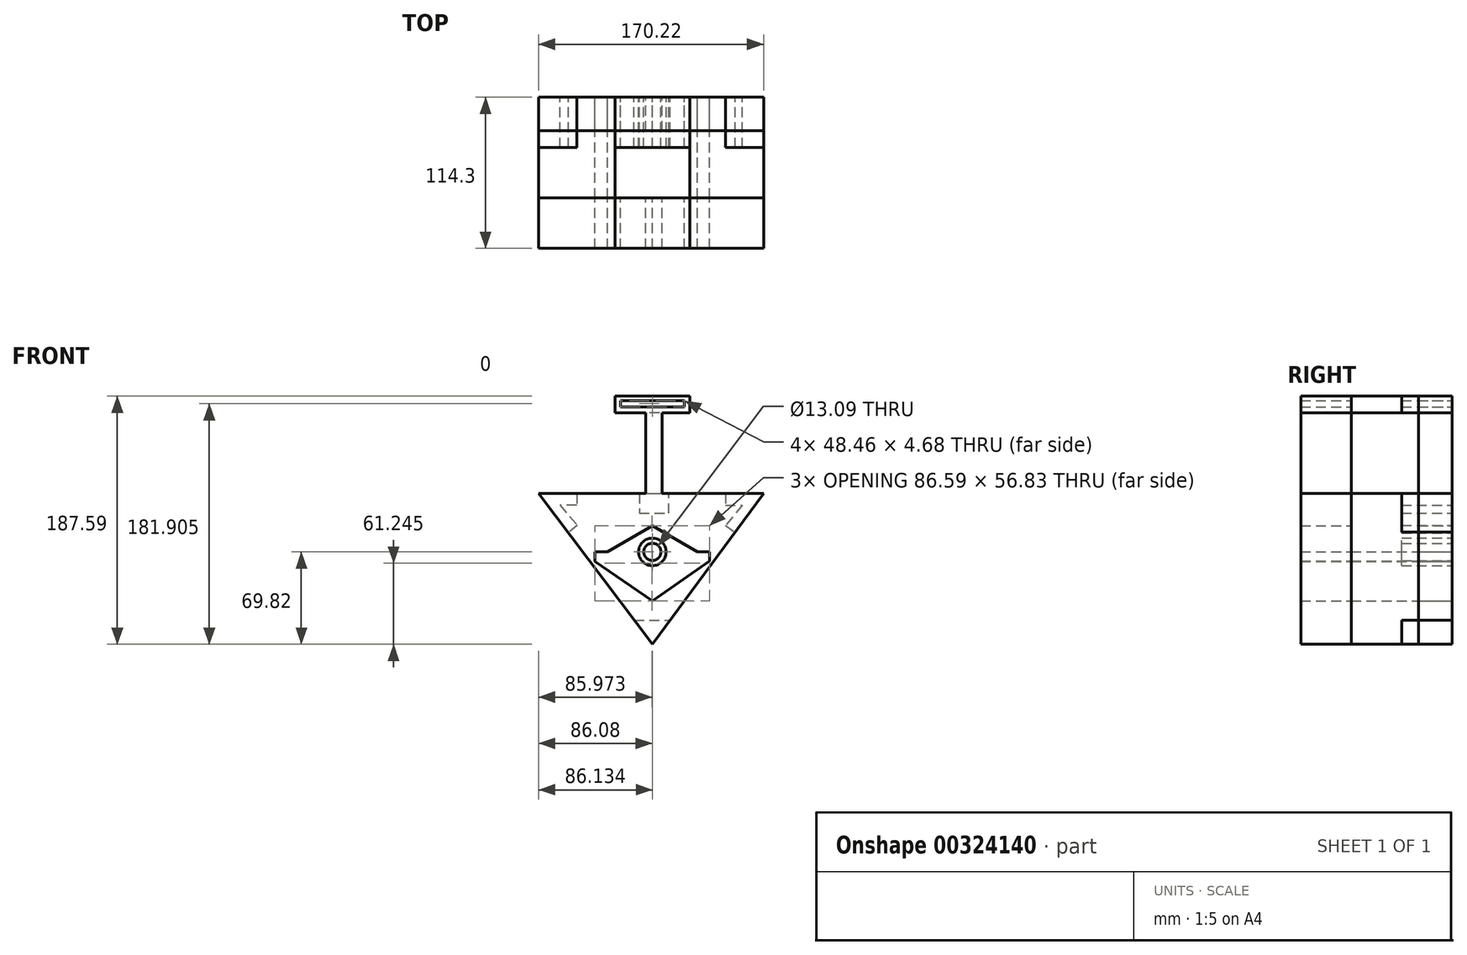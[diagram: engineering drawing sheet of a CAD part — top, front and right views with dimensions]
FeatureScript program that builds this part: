
annotation { "Feature Type Name" : "Feature", "Feature Type Description" : "" }
export const myFeature = defineFeature(function(context is Context, id is Id, definition is map)
    precondition{}
    {
        {
            var Q0;
            Q0=qCreatedBy(makeId("Front.planeOp"),FACE);
            var sketch = newSketch(context, id + "F0", { "sketchPlane" : qUnion([Q0])});
            skLineSegment(sketch, "E0", {"start": v(84.14, 44.25) * mm, "end": v(0, -69.82) * mm});
            skLineSegment(sketch, "E1", {"start": v(0, -69.82) * mm, "end": v(-86.08, 44.25) * mm});
            skLineSegment(sketch, "E2", {"start": v(-86.08, 44.25) * mm, "end": v(84.14, 44.25) * mm});
            skLineSegment(sketch, "E3", {"start": v(-13.76, -51.58) * mm, "end": v(13.45, -51.58) * mm});
            skLineSegment(sketch, "E4", {"start": v(55.26, 44.25) * mm, "end": v(55.26, 35.37) * mm});
            skLineSegment(sketch, "E5", {"start": v(55.26, 35.37) * mm, "end": v(67.96, 35.37) * mm});
            skLineSegment(sketch, "E6", {"start": v(67.96, 35.37) * mm, "end": v(55.3, 20.13) * mm});
            skLineSegment(sketch, "E7", {"start": v(55.3, 20.13) * mm, "end": v(62.45, 14.85) * mm});
            skLineSegment(sketch, "E8", {"start": v(-57.2, 44.25) * mm, "end": v(-57.2, 35.37) * mm});
            skLineSegment(sketch, "E9", {"start": v(-57.2, 35.37) * mm, "end": v(-69.9, 35.37) * mm});
            skLineSegment(sketch, "E10", {"start": v(-69.9, 35.37) * mm, "end": v(-56.76, 20.13) * mm});
            skLineSegment(sketch, "E11", {"start": v(-56.76, 20.13) * mm, "end": v(-63.5, 14.32) * mm});
            skCircle(sketch, "E12", {"center": v(0, 0) * mm, "radius": 10.43 * mm});
            skCircle(sketch, "E13", {"center": v(0, 0) * mm, "radius": 6.55 * mm});
            skLineSegment(sketch, "E14", {"start": v(-126.97, 0) * mm, "end": v(136.35, 0) * mm, "construction": true});
            skLineSegment(sketch, "E15", {"start": v(0, 91.75) * mm, "end": v(0, -85.84) * mm, "construction": true});
            skLineSegment(sketch, "E16", {"start": v(-9.84, 44.25) * mm, "end": v(-9.84, 29.26) * mm});
            skLineSegment(sketch, "E17", {"start": v(-9.84, 29.26) * mm, "end": v(12.4, 29.26) * mm});
            skLineSegment(sketch, "E18", {"start": v(12.4, 29.26) * mm, "end": v(12.4, 44.25) * mm});
            skPoint(sketch, "E19", {"position": v(0, 44.25) * mm});
            skLineSegment(sketch, "E20", {"start": v(-5.08, 44.25) * mm, "end": v(-5.08, 105.28) * mm});
            skLineSegment(sketch, "E21", {"start": v(-5.08, 105.28) * mm, "end": v(7.33, 105.28) * mm});
            skLineSegment(sketch, "E22", {"start": v(7.33, 105.28) * mm, "end": v(7.33, 44.25) * mm});
            skLineSegment(sketch, "E23", {"start": v(-5.08, 105.28) * mm, "end": v(-28.17, 105.28) * mm});
            skLineSegment(sketch, "E24", {"start": v(-28.17, 105.28) * mm, "end": v(-28.17, 117.77) * mm});
            skLineSegment(sketch, "E25", {"start": v(-28.17, 117.77) * mm, "end": v(28.31, 117.77) * mm});
            skLineSegment(sketch, "E26", {"start": v(28.31, 117.77) * mm, "end": v(28.31, 105.28) * mm});
            skLineSegment(sketch, "E27", {"start": v(28.31, 105.28) * mm, "end": v(7.33, 105.28) * mm});
            skLineSegment(sketch, "E28", {"start": v(-33.85, 0) * mm, "end": v(0, 19.84) * mm});
            skLineSegment(sketch, "E29", {"start": v(0, 19.84) * mm, "end": v(34, 0) * mm});
            skLineSegment(sketch, "E30", {"start": v(34, 0) * mm, "end": v(0, -20.6) * mm});
            skLineSegment(sketch, "E31", {"start": v(0, -20.6) * mm, "end": v(-33.85, 0) * mm});
            skLineSegment(sketch, "E32", {"start": v(-24.18, 114.42) * mm, "end": v(24.28, 114.42) * mm});
            skLineSegment(sketch, "E33", {"start": v(24.28, 114.42) * mm, "end": v(24.28, 109.75) * mm});
            skLineSegment(sketch, "E34", {"start": v(-24.18, 114.42) * mm, "end": v(-24.18, 109.75) * mm});
            skLineSegment(sketch, "E35", {"start": v(-24.18, 109.75) * mm, "end": v(24.28, 109.75) * mm});
            skLineSegment(sketch, "E36", {"start": v(-24.18, 44.25) * mm, "end": v(-24.18, 29.26) * mm});
            skLineSegment(sketch, "E37", {"start": v(-24.18, 29.26) * mm, "end": v(-45.5, 29.26) * mm});
            skLineSegment(sketch, "E38", {"start": v(-45.5, 29.26) * mm, "end": v(-33.83, 17.6) * mm});
            skLineSegment(sketch, "E39", {"start": v(-33.83, 17.6) * mm, "end": v(-48.6, 8.97) * mm});
            skLineSegment(sketch, "E40", {"start": v(-48.6, 8.97) * mm, "end": v(-33.85, 0) * mm});
            skLineSegment(sketch, "E41", {"start": v(-43.4, -7.1) * mm, "end": v(0, -36.99) * mm});
            skLineSegment(sketch, "E42", {"start": v(26.75, 44.25) * mm, "end": v(26.75, 29.26) * mm});
            skLineSegment(sketch, "E43", {"start": v(26.75, 29.26) * mm, "end": v(48.08, 29.26) * mm});
            skLineSegment(sketch, "E44", {"start": v(48.08, 29.26) * mm, "end": v(31.15, 15.8) * mm});
            skLineSegment(sketch, "E45", {"start": v(31.15, 15.8) * mm, "end": v(47.03, 11.32) * mm});
            skLineSegment(sketch, "E46", {"start": v(47.03, 11.32) * mm, "end": v(34, 0) * mm});
            skLineSegment(sketch, "E47", {"start": v(43.2, -6.78) * mm, "end": v(0, -36.99) * mm});
            skLineSegment(sketch, "E48", {"start": v(-43.4, -7.1) * mm, "end": v(-43.4, 0) * mm});
            skLineSegment(sketch, "E49", {"start": v(-43.4, 0) * mm, "end": v(-33.85, 0) * mm});
            skLineSegment(sketch, "E50", {"start": v(-41.23, 0) * mm, "end": v(-33.85, 0) * mm});
            skPoint(sketch, "E50.startSnap0", {"position": v(-41.23, 4.49) * mm});
            skLineSegment(sketch, "E51", {"start": v(43.2, -6.78) * mm, "end": v(43.2, 0) * mm});
            skLineSegment(sketch, "E52", {"start": v(43.2, 0) * mm, "end": v(34, 0) * mm});
            skLineSegment(sketch, "E53", {"start": v(-41.23, 0) * mm, "end": v(-52.68, 0) * mm});
            skLineSegment(sketch, "E54", {"start": v(43.2, 0) * mm, "end": v(51.5, 0) * mm});
            skSolve(sketch);
        }
        {
            var Q0;
            {var subQ0=sQuery(id+"F0.wireOp",EDGE,"E4");Q0=makeQuery(id+"F0.imprint","IMPRINT",FACE,{"disambiguationData":[TD([[makeQuery(id+"F0.imprint","IMPRINT",EDGE,{"derivedFrom":subQ0}),1.0]])]});}
            var Q1;
            {var subQ3=sQuery(id+"F0.wireOp",EDGE,"E3");Q1=makeQuery(id+"F0.imprint","IMPRINT",FACE,{"disambiguationData":[TD([[makeQuery(id+"F0.imprint","IMPRINT",EDGE,{"derivedFrom":subQ3}),-1.0]])]});}
            var Q2;
            {var subQ3=sQuery(id+"F0.wireOp",EDGE,"E8");Q2=makeQuery(id+"F0.imprint","IMPRINT",FACE,{"disambiguationData":[TD([[makeQuery(id+"F0.imprint","IMPRINT",EDGE,{"derivedFrom":subQ3}),-1.0]])]});}
            var Q3;
            {var subQ0=sQuery(id+"F0.wireOp",EDGE,"E16");Q3=makeQuery(id+"F0.imprint","IMPRINT",FACE,{"disambiguationData":[TD([[makeQuery(id+"F0.imprint","IMPRINT",EDGE,{"derivedFrom":subQ0}),1.0]])]});}
            var Q4;
            Q4=makeQuery(id+"F0.imprint","IMPRINT",FACE,{"disambiguationData":[TD([[makeQuery(id+"F0.imprint","IMPRINT",EDGE,{"derivedFrom":sQuery(id+"F0.wireOp",EDGE,"E21")}),1.0]])]});
            var Q5;
            Q5=makeQuery(id+"F0.imprint","IMPRINT",FACE,{"disambiguationData":[TD([[makeQuery(id+"F0.imprint","IMPRINT",EDGE,{"derivedFrom":sQuery(id+"F0.wireOp",EDGE,"E12")}),1.0]])]});
            extrude(context, id + "F1", {"entities" : qUnion([Q0, Q1, Q2, Q3, Q4, Q5]), "depth" : 38.1 * mm});
        }
        {
            var Q0;
            Q0 = qSketchRegion(id + "F0", true);
            extrude(context, id + "F2", {"entities" : qUnion([Q0]), "depth" : 76.2 * mm});
        }
        {
            var Q0;
            Q0=makeQuery(id+"F2.opExtrude","CAP_FACE",FACE,{"disambiguationData":[OSD([sQuery(id+"F0.wireOp",EDGE,"E0"),sQuery(id+"F0.wireOp",EDGE,"E1"),sQuery(id+"F0.wireOp",EDGE,"E2"),sQuery(id+"F0.wireOp",EDGE,"E20"),sQuery(id+"F0.wireOp",EDGE,"E22"),sQuery(id+"F0.wireOp",EDGE,"E23"),sQuery(id+"F0.wireOp",EDGE,"E24"),sQuery(id+"F0.wireOp",EDGE,"E25"),sQuery(id+"F0.wireOp",EDGE,"E26"),sQuery(id+"F0.wireOp",EDGE,"E27"),sQuery(id+"F0.wireOp",EDGE,"E28"),sQuery(id+"F0.wireOp",EDGE,"E29"),sQuery(id+"F0.wireOp",EDGE,"E32"),sQuery(id+"F0.wireOp",EDGE,"E33"),sQuery(id+"F0.wireOp",EDGE,"E34"),sQuery(id+"F0.wireOp",EDGE,"E35"),sQuery(id+"F0.wireOp",EDGE,"E41"),sQuery(id+"F0.wireOp",EDGE,"E47"),sQuery(id+"F0.wireOp",EDGE,"E48"),sQuery(id+"F0.wireOp",EDGE,"E50"),sQuery(id+"F0.wireOp",EDGE,"E51"),sQuery(id+"F0.wireOp",EDGE,"E52"),sQuery(id+"F0.wireOp",EDGE,"E53")])],"isStart":false});
            extrude(context, id + "F3", {"entities" : qUnion([Q0]), "depth" : 38.1 * mm});
        }
        {
            var Q0;
            Q0 = qSketchRegion(id + "F0", true);
            extrude(context, id + "F4", {"entities" : qUnion([Q0]), "depth" : 25.4 * mm});
        }
    });
